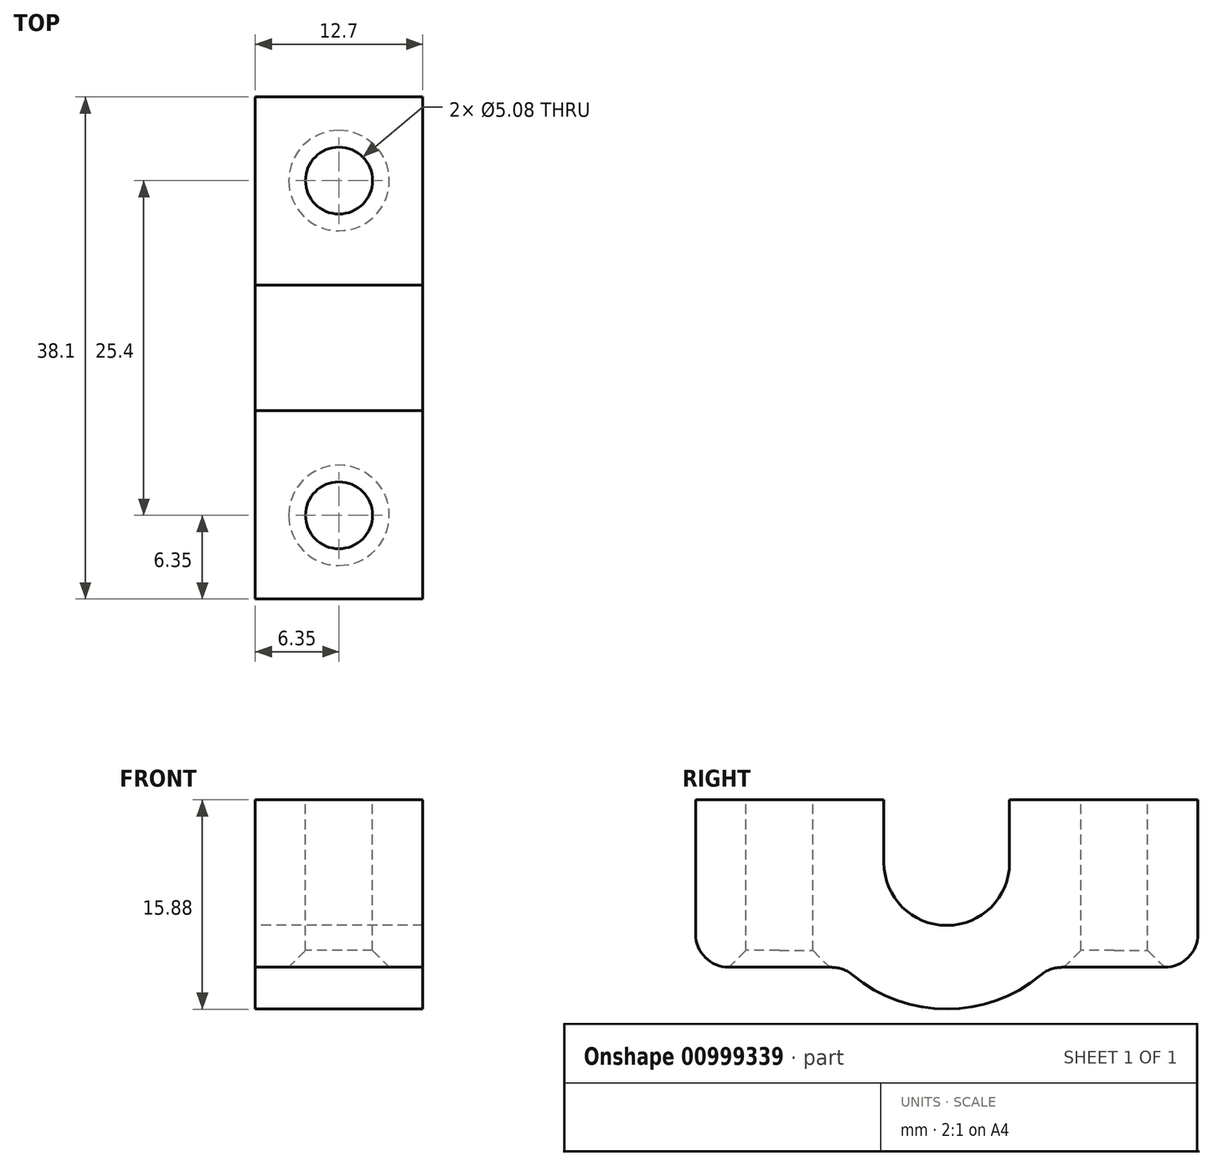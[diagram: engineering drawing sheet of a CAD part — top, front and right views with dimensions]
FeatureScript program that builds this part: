
annotation { "Feature Type Name" : "Feature", "Feature Type Description" : "" }
export const myFeature = defineFeature(function(context is Context, id is Id, definition is map)
    precondition{}
    {
        {
            var Q0;
            Q0=qCreatedBy(makeId("Top.planeOp"),FACE);
            var sketch = newSketch(context, id + "F0", { "sketchPlane" : qUnion([Q0])});
            skArc(sketch, "E0", {"start": v(0, 9.98) * mm, "mid": v(4.85, 0) * mm, "end": v(0, -9.98) * mm});
            skLineSegment(sketch, "E1", {"start": v(0, 19.05) * mm, "end": v(12.7, 19.05) * mm, "construction": true});
            skLineSegment(sketch, "E2", {"start": v(12.7, 19.05) * mm, "end": v(12.7, -19.05) * mm, "construction": true});
            skLineSegment(sketch, "E3", {"start": v(12.7, -19.05) * mm, "end": v(0, -19.05) * mm, "construction": true});
            skCircle(sketch, "E4", {"center": v(6.35, 12.7) * mm, "radius": 2.54 * mm});
            skCircle(sketch, "E5", {"center": v(6.35, -12.7) * mm, "radius": 2.54 * mm});
            skCircle(sketch, "E6", {"center": v(6.35, 12.7) * mm, "radius": 3.81 * mm, "construction": true});
            skCircle(sketch, "E7", {"center": v(6.35, -12.7) * mm, "radius": 3.81 * mm, "construction": true});
            skLineSegment(sketch, "E8", {"start": v(0, 19.05) * mm, "end": v(0, 9.98) * mm, "construction": true});
            skLineSegment(sketch, "E9.trimOffspring", {"start": v(0, -9.98) * mm, "end": v(0, -19.05) * mm, "construction": true});
            skLineSegment(sketch, "E10", {"start": v(0, 9.98) * mm, "end": v(0, -9.98) * mm});
            skSolve(sketch);
        }
        {
            var Q0;
            Q0=qCreatedBy(makeId("Right.planeOp"),FACE);
            var sketch = newSketch(context, id + "F1", { "sketchPlane" : qUnion([Q0])});
            skCircle(sketch, "E11", {"center": v(0, -4.76) * mm, "radius": 4.76 * mm, "construction": true});
            skLineSegment(sketch, "E12", {"start": v(4.76, -4.76) * mm, "end": v(4.76, 0) * mm});
            skLineSegment(sketch, "E13", {"start": v(4.76, 0) * mm, "end": v(19.05, 0) * mm});
            skLineSegment(sketch, "E14", {"start": v(19.05, 0) * mm, "end": v(19.05, -12.7) * mm});
            skLineSegment(sketch, "E15", {"start": v(19.05, -12.7) * mm, "end": v(7.78, -12.7) * mm});
            skLineSegment(sketch, "E16", {"start": v(-19.05, -12.7) * mm, "end": v(-19.05, 0) * mm});
            skLineSegment(sketch, "E17", {"start": v(-19.05, 0) * mm, "end": v(-4.76, 0) * mm});
            skLineSegment(sketch, "E18", {"start": v(-4.76, 0) * mm, "end": v(-4.76, -4.76) * mm});
            skArc(sketch, "E19", {"start": v(4.76, -4.76) * mm, "mid": v(0, -9.53) * mm, "end": v(-4.76, -4.76) * mm});
            skArc(sketch, "E20", {"start": v(7.78, -12.7) * mm, "mid": v(0, -15.88) * mm, "end": v(-7.78, -12.7) * mm});
            skLineSegment(sketch, "E21.trimOffspring", {"start": v(-7.78, -12.7) * mm, "end": v(-19.05, -12.7) * mm});
            skLineSegment(sketch, "E22", {"start": v(-50.92, -6.35) * mm, "end": v(68.3, -6.35) * mm, "construction": true});
            skLineSegment(sketch, "E23", {"start": v(-68.93, -20.64) * mm, "end": v(68.77, -20.64) * mm, "construction": true});
            skLineSegment(sketch, "E24", {"start": v(-73.08, -4.76) * mm, "end": v(71.16, -4.76) * mm, "construction": true});
            skSolve(sketch);
        }
        {
            var Q0;
            Q0 = qSketchRegion(id + "F1", true);
            extrude(context, id + "F2", {"entities" : qUnion([Q0]), "depth" : 12.7 * mm, "offsetDistance" : 25.4 * mm});
        }
        {
            var Q0;
            Q0=makeQuery(id+"F0.imprint","IMPRINT",FACE,{"disambiguationData":[TD([[makeQuery(id+"F0.imprint","IMPRINT",EDGE,{"derivedFrom":sQuery(id+"F0.wireOp",EDGE,"E4")}),1.0]])]});
            var Q1;
            Q1=makeQuery(id+"F0.imprint","IMPRINT",FACE,{"disambiguationData":[TD([[makeQuery(id+"F0.imprint","IMPRINT",EDGE,{"derivedFrom":sQuery(id+"F0.wireOp",EDGE,"E5")}),1.0]])]});
            var Q2;
            Q2=makeQuery(id+"F0.imprint","IMPRINT",FACE,{"disambiguationData":[TD([[makeQuery(id+"F0.imprint","IMPRINT",EDGE,{"derivedFrom":sQuery(id+"F0.wireOp",EDGE,"E0")}),-1.0]])]});
            extrude(context, id + "F3", {"entities" : qUnion([Q0, Q1, Q2]), "operationType" : NewBodyOperationType.REMOVE, "oppositeDirection" : true, "depth" : 25.4 * mm, "offsetDistance" : 25.4 * mm});
        }
        {
            var Q0;
            Q0=makeQuery(id+"F2.opExtrude","SWEPT_EDGE",EDGE,{"disambiguationData":[OSD([sQuery(id+"F1.wireOp",EDGE,"E14"),sQuery(id+"F1.wireOp",EDGE,"E15")])]});
            var Q1;
            Q1=makeQuery(id+"F2.opExtrude","SWEPT_EDGE",EDGE,{"disambiguationData":[OSD([sQuery(id+"F1.wireOp",EDGE,"E16"),sQuery(id+"F1.wireOp",EDGE,"E21.trimOffspring")])]});
            var Q2;
            Q2=makeQuery(id+"F2.opExtrude","SWEPT_EDGE",EDGE,{"disambiguationData":[OSD([sQuery(id+"F1.wireOp",EDGE,"E15"),sQuery(id+"F1.wireOp",EDGE,"E20")])]});
            var Q3;
            Q3=makeQuery(id+"F2.opExtrude","SWEPT_EDGE",EDGE,{"disambiguationData":[OSD([sQuery(id+"F1.wireOp",EDGE,"E20"),sQuery(id+"F1.wireOp",EDGE,"E21.trimOffspring")])]});
            fillet(context, id + "F4", {"entities" : qUnion([Q0, Q1, Q2, Q3]), "tangentPropagation" : true, "radius" : 2.54 * mm, "defaultsChanged" : false, "vertexSettings" : [], "allowEdgeOverflow" : false});
        }
        {
            var Q0;
            Q0=makeQuery(id+"F3.boolean.opBoolean","INTERSECT",EDGE,{"derivedFrom":[makeQuery(id+"F2.opExtrude","SWEPT_FACE",FACE,{"disambiguationData":[OSD([sQuery(id+"F1.wireOp",EDGE,"E15")])]}),makeQuery(id+"F3.opExtrude","SWEPT_FACE",FACE,{"disambiguationData":[OSD([sQuery(id+"F0.wireOp",EDGE,"E4")])]})]});
            var Q1;
            Q1=makeQuery(id+"F3.boolean.opBoolean","INTERSECT",EDGE,{"derivedFrom":[makeQuery(id+"F2.opExtrude","SWEPT_FACE",FACE,{"disambiguationData":[OSD([sQuery(id+"F1.wireOp",EDGE,"E21.trimOffspring")])]}),makeQuery(id+"F3.opExtrude","SWEPT_FACE",FACE,{"disambiguationData":[OSD([sQuery(id+"F0.wireOp",EDGE,"E5")])]})]});
            chamfer(context, id + "F5", {"entities" : qUnion([Q0, Q1]), "width" : 1.27 * mm, "tangentPropagation" : true});
        }
    });
